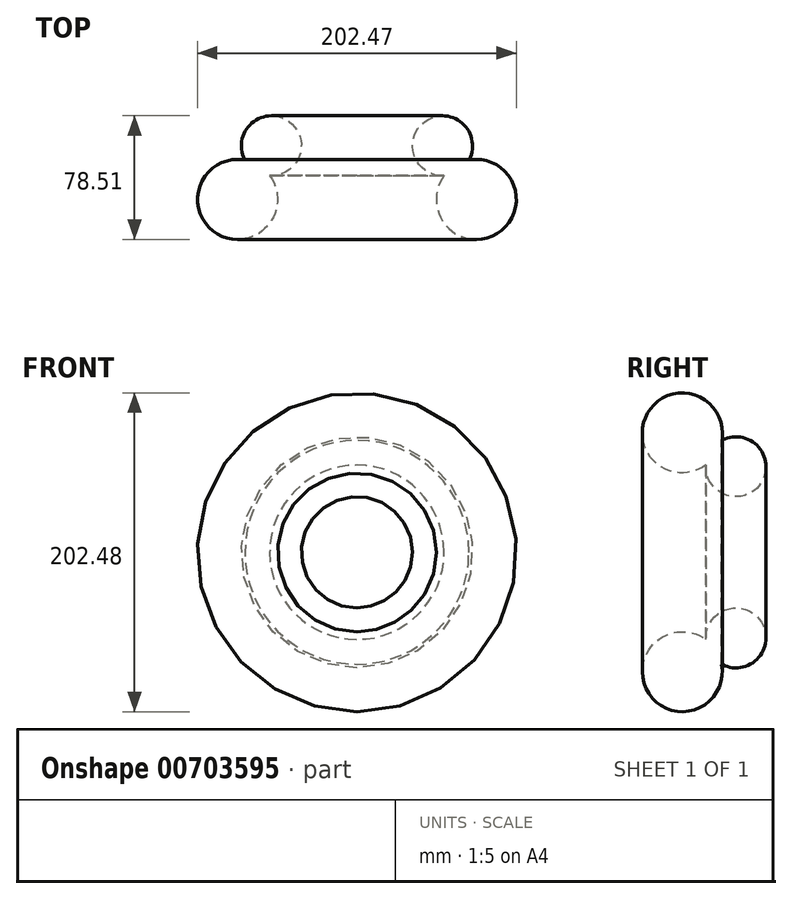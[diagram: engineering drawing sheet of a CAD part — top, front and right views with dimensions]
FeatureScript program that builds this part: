
annotation { "Feature Type Name" : "Feature", "Feature Type Description" : "" }
export const myFeature = defineFeature(function(context is Context, id is Id, definition is map)
    precondition{}
    {
        {
            var Q0;
            Q0=qCreatedBy(makeId("Top.planeOp"),FACE);
            var sketch = newSketch(context, id + "F0", { "sketchPlane" : qUnion([Q0])});
            skCircle(sketch, "E0", {"center": v(0, 0) * mm, "radius": 25.4 * mm});
            skCircle(sketch, "E1", {"center": v(-21.47, 34.06) * mm, "radius": 19.05 * mm});
            skSolve(sketch);
        }
        {
            var Q0;
            {var subQ0=sQuery(id+"F0.wireOp",EDGE,"E1");var subQ1=sQuery(id+"F0.wireOp",EDGE,"E0");var subQ2=makeQuery(id+"F0.imprint","INTERSECT",VERTEX,{"disambiguationData":[OD(0.0)],"derivedFrom":[subQ1,subQ0]});Q0=makeQuery(id+"F0.imprint","IMPRINT",FACE,{"disambiguationData":[TD([[makeQuery(id+"F0.imprint","IMPRINT",EDGE,{"disambiguationData":[TD([[subQ2,-1.0]])],"derivedFrom":subQ1}),1.0]])]});}
            var sketch = newSketch(context, id + "F1", { "sketchPlane" : qUnion([Q0])});
            skLineSegment(sketch, "E2", {"start": v(-75.84, 0) * mm, "end": v(-75.84, 27.77) * mm});
            skSolve(sketch);
        }
        {
            var Q0;
            {var subQ0=sQuery(id+"F0.wireOp",EDGE,"E1");var subQ1=sQuery(id+"F0.wireOp",EDGE,"E0");var subQ2=makeQuery(id+"F0.imprint","INTERSECT",VERTEX,{"disambiguationData":[OD(0.0)],"derivedFrom":[subQ1,subQ0]});Q0=makeQuery(id+"F0.imprint","IMPRINT",FACE,{"disambiguationData":[TD([[makeQuery(id+"F0.imprint","IMPRINT",EDGE,{"disambiguationData":[TD([[subQ2,1.0]])],"derivedFrom":subQ1}),-1.0]])]});}
            var Q1;
            {var subQ0=sQuery(id+"F0.wireOp",EDGE,"E1");var subQ1=sQuery(id+"F0.wireOp",EDGE,"E0");var subQ2=makeQuery(id+"F0.imprint","INTERSECT",VERTEX,{"disambiguationData":[OD(0.0)],"derivedFrom":[subQ1,subQ0]});Q1=makeQuery(id+"F0.imprint","IMPRINT",FACE,{"disambiguationData":[TD([[makeQuery(id+"F0.imprint","IMPRINT",EDGE,{"disambiguationData":[TD([[subQ2,1.0]])],"derivedFrom":subQ1}),1.0]])]});}
            var Q2;
            {var subQ0=sQuery(id+"F0.wireOp",EDGE,"E1");var subQ1=sQuery(id+"F0.wireOp",EDGE,"E0");var subQ2=makeQuery(id+"F0.imprint","INTERSECT",VERTEX,{"disambiguationData":[OD(0.0)],"derivedFrom":[subQ1,subQ0]});Q2=makeQuery(id+"F0.imprint","IMPRINT",FACE,{"disambiguationData":[TD([[makeQuery(id+"F0.imprint","IMPRINT",EDGE,{"disambiguationData":[TD([[subQ2,-1.0]])],"derivedFrom":subQ1}),1.0]])]});}
            var Q3;
            Q3=sQuery(id+"F1.wireOp",EDGE,"E2");
            revolve(context, id + "F2", {"surfaceOperationType" : NewSurfaceOperationType.NEW, "entities" : qUnion([Q0, Q1, Q2]), "axis" : qUnion([Q3]), "revolveType" : RevolveType.FULL});
        }
    });
